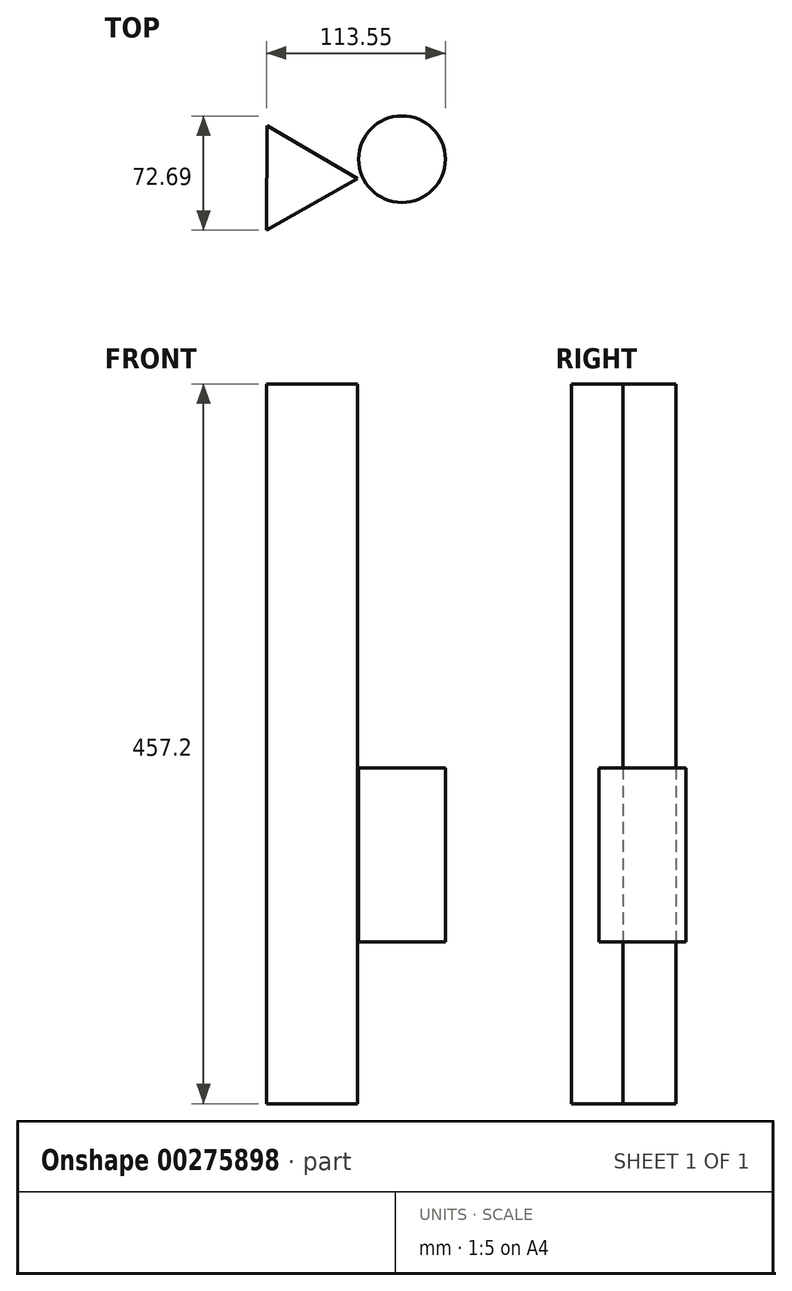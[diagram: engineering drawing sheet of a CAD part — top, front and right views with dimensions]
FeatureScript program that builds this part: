
annotation { "Feature Type Name" : "Feature", "Feature Type Description" : "" }
export const myFeature = defineFeature(function(context is Context, id is Id, definition is map)
    precondition{}
    {
        {
            var Q0;
            Q0=qCreatedBy(makeId("Top.planeOp"),FACE);
            var sketch = newSketch(context, id + "F0", { "sketchPlane" : qUnion([Q0])});
            skCircle(sketch, "E0.cCircle", {"center": v(-56.88, 36.4) * mm, "radius": 19.19 * mm, "construction": true});
            skLineSegment(sketch, "E0.0", {"start": v(-18.5, 36.14) * mm, "end": v(-76.3, 3.3) * mm});
            skLineSegment(sketch, "E0.1", {"start": v(-76.3, 3.3) * mm, "end": v(-75.84, 69.77) * mm});
            skLineSegment(sketch, "E0.2", {"start": v(-75.84, 69.77) * mm, "end": v(-18.5, 36.14) * mm});
            skPoint(sketch, "E0.0.midPoint", {"position": v(-47.4, 19.72) * mm});
            skSolve(sketch);
        }
        {
            var Q0;
            Q0=makeQuery(id+"F0.imprint","IMPRINT",FACE,{"disambiguationData":[TD([[makeQuery(id+"F0.imprint","IMPRINT",EDGE,{"derivedFrom":sQuery(id+"F0.wireOp",EDGE,"E0.0")}),-1.0]])]});
            extrude(context, id + "F1", {"entities" : qUnion([Q0]), "depth" : 269.24 * mm, "hasSecondDirection" : true, "secondDirectionOppositeDirection" : true, "secondDirectionDepth" : 187.96 * mm});
        }
        {
            var Q0;
            Q0=qCreatedBy(makeId("Top.planeOp"),FACE);
            var sketch = newSketch(context, id + "F2", { "sketchPlane" : qUnion([Q0])});
            skCircle(sketch, "E1", {"center": v(9.73, 48.47) * mm, "radius": 27.52 * mm});
            skSolve(sketch);
        }
        {
            var Q0;
            Q0=makeQuery(id+"F2.imprint","IMPRINT",FACE,{"disambiguationData":[TD([[makeQuery(id+"F2.imprint","IMPRINT",EDGE,{"derivedFrom":sQuery(id+"F2.wireOp",EDGE,"E1")}),1.0]])]});
            extrude(context, id + "F3", {"entities" : qUnion([Q0]), "depth" : 25.4 * mm, "hasSecondDirection" : true, "secondDirectionOppositeDirection" : true, "secondDirectionDepth" : 85.1 * mm});
        }
    });
